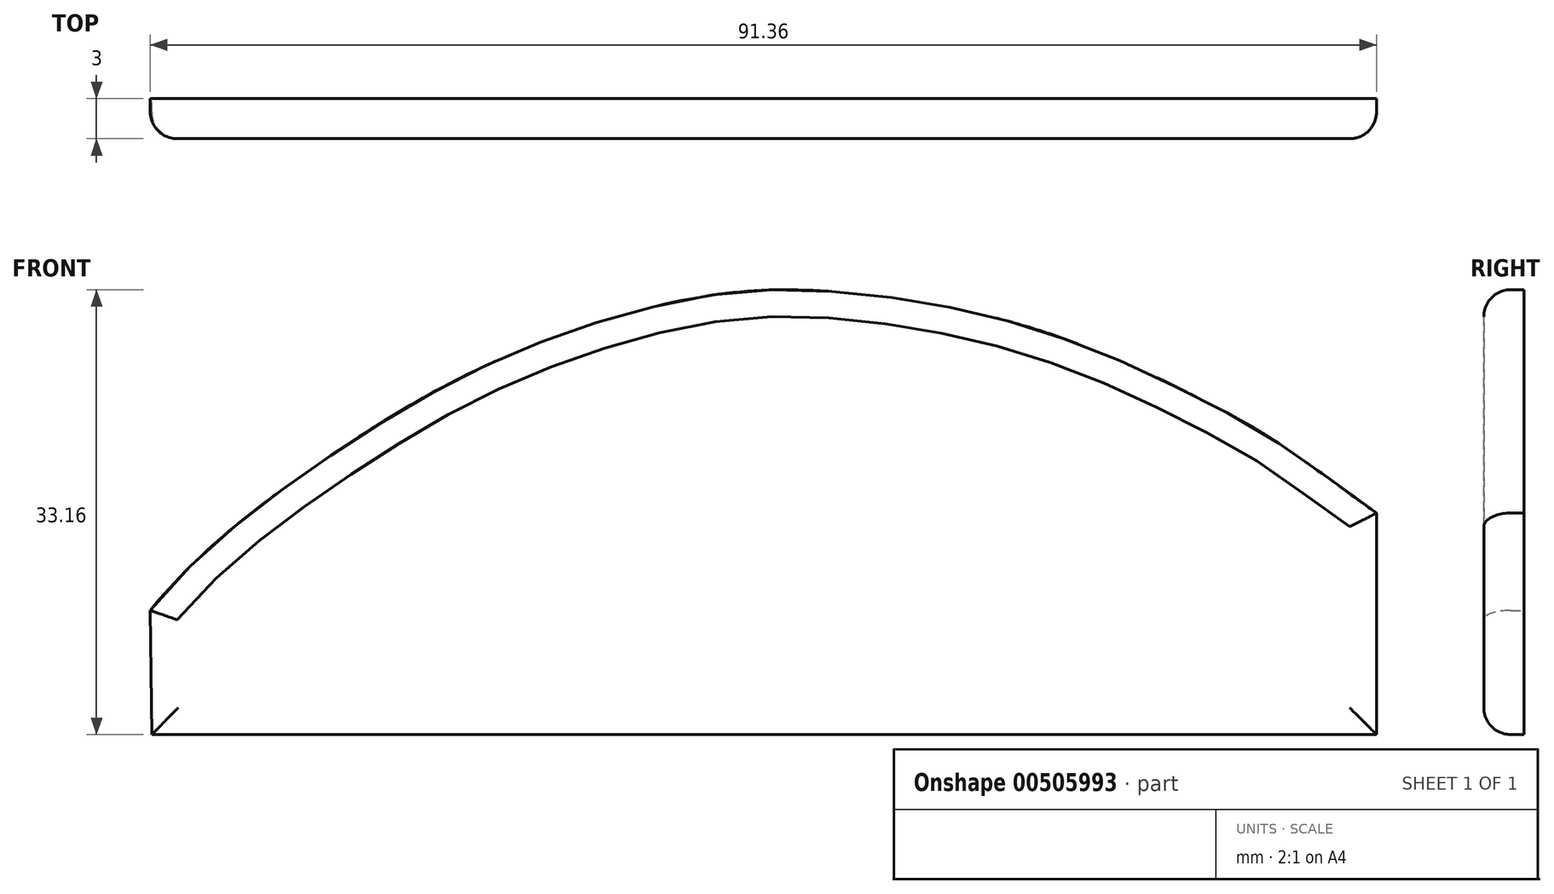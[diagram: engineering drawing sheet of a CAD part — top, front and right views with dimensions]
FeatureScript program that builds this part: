
annotation { "Feature Type Name" : "Feature", "Feature Type Description" : "" }
export const myFeature = defineFeature(function(context is Context, id is Id, definition is map)
    precondition{}
    {
        {
            var Q0;
            Q0=qCreatedBy(makeId("Front.planeOp"),FACE);
            var sketch = newSketch(context, id + "F0", { "sketchPlane" : qUnion([Q0])});
            skLineSegment(sketch, "E0", {"start": v(-45.37, -9.64) * mm, "end": v(45.88, -9.64) * mm});
            skLineSegment(sketch, "E1", {"start": v(-45.37, -9.64) * mm, "end": v(-45.48, -0.38) * mm});
            skLineSegment(sketch, "E2", {"start": v(45.88, -9.64) * mm, "end": v(45.88, 6.9) * mm});
            skFitSpline(sketch, "E3", {"points": [v(-45.48, -0.38) * mm, v(-32.3, 10.97) * mm, v(-19.05, 18.51) * mm, v(-5.05, 22.88) * mm, v(5.57, 23.37) * mm, v(21.64, 20.2) * mm, v(34.33, 14.55) * mm, v(39.75, 11.28) * mm, v(45.88, 6.9) * mm, v(45.88, 6.9) * mm], "startDerivative": vector(73.93, 92.2) * mm, "endDerivative": vector(42.14, -36.84) * mm});
            skSolve(sketch);
        }
        {
            var Q0;
            {var subQ0=sQuery(id+"F0.wireOp",EDGE,"E0");Q0=makeQuery(id+"F0.imprint","IMPRINT",FACE,{"disambiguationData":[TD([[makeQuery(id+"F0.imprint","IMPRINT",EDGE,{"derivedFrom":subQ0}),1.0]])]});}
            extrude(context, id + "F1", {"entities" : qUnion([Q0]), "depth" : 3 * mm, "offsetDistance" : 25 * mm});
        }
        {
            var Q0;
            Q0=makeQuery(id+"F1.opExtrude","CAP_EDGE",EDGE,{"disambiguationData":[OSD([sQuery(id+"F0.wireOp",EDGE,"E3")])],"isStart":false});
            var Q1;
            Q1=makeQuery(id+"F1.opExtrude","CAP_EDGE",EDGE,{"disambiguationData":[OSD([sQuery(id+"F0.wireOp",EDGE,"E1")])],"isStart":false});
            var Q2;
            Q2=makeQuery(id+"F1.opExtrude","CAP_EDGE",EDGE,{"disambiguationData":[OSD([sQuery(id+"F0.wireOp",EDGE,"E0")])],"isStart":false});
            var Q3;
            Q3=makeQuery(id+"F1.opExtrude","CAP_EDGE",EDGE,{"disambiguationData":[OSD([sQuery(id+"F0.wireOp",EDGE,"E2")])],"isStart":false});
            fillet(context, id + "F2", {"entities" : qUnion([Q0, Q1, Q2, Q3]), "radius" : 2 * mm, "tangentPropagation" : true, "allowEdgeOverflow" : false});
        }
    });
